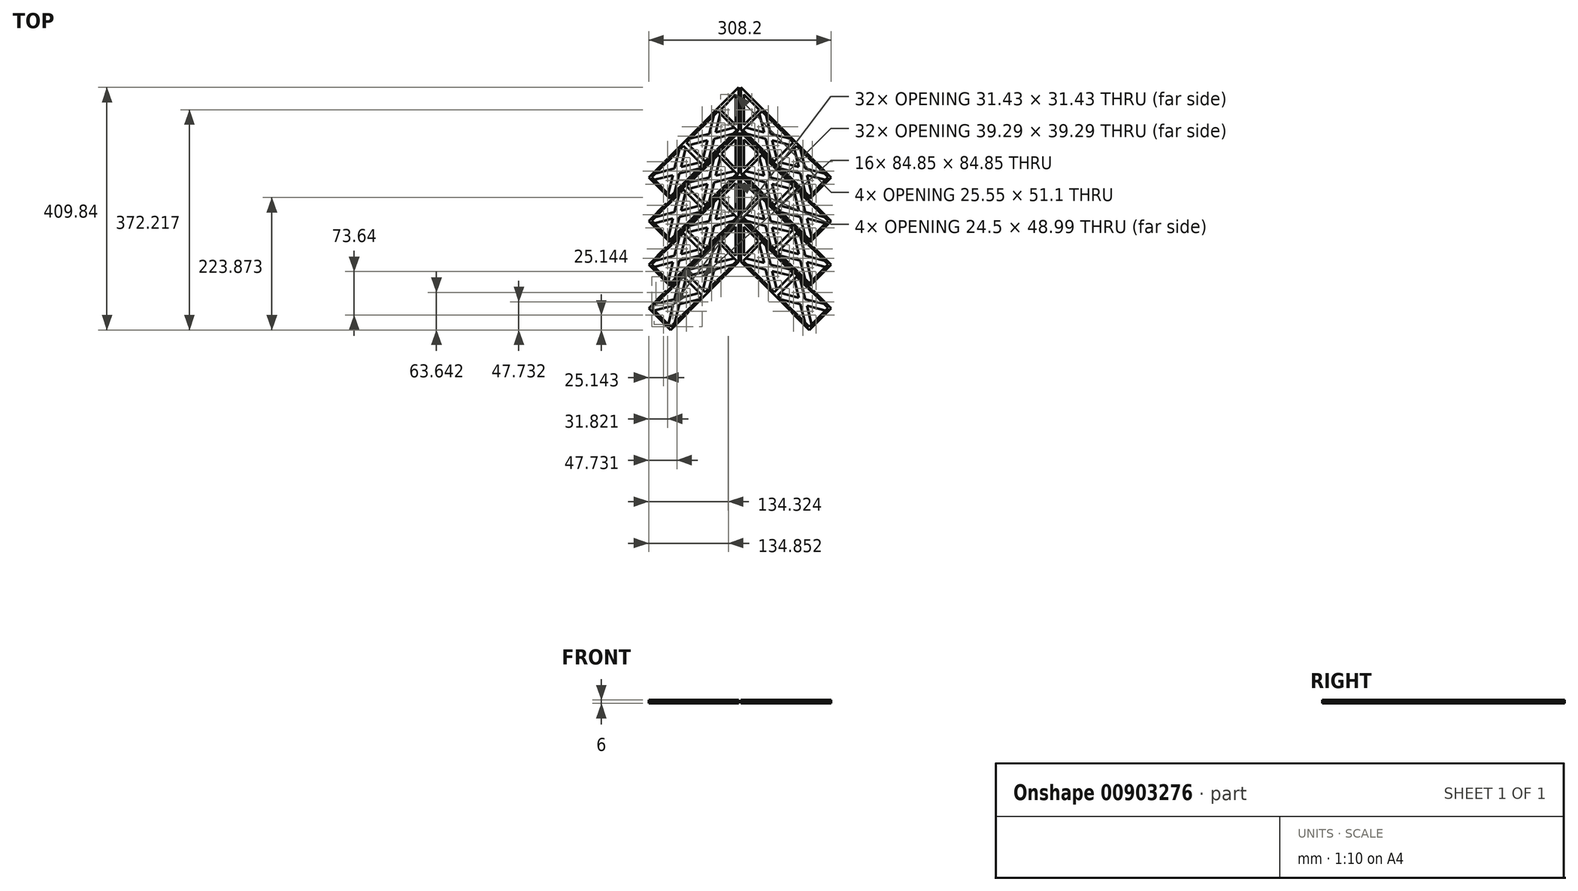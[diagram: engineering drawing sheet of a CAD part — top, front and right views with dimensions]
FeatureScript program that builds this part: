
annotation { "Feature Type Name" : "Feature", "Feature Type Description" : "" }
export const myFeature = defineFeature(function(context is Context, id is Id, definition is map)
    precondition{}
    {
        {
            var Q0;
            Q0=qCreatedBy(makeId("Top.planeOp"),FACE);
            var sketch = newSketch(context, id + "F0", { "sketchPlane" : qUnion([Q0])});
            skLineSegment(sketch, "E0", {"start": v(0, 0) * mm, "end": v(-31.82, -31.82) * mm});
            skLineSegment(sketch, "E1", {"start": v(-31.82, -31.82) * mm, "end": v(-2, -61.64) * mm});
            skLineSegment(sketch, "E2", {"start": v(-2, -208.92) * mm, "end": v(-30.76, -180.16) * mm});
            skLineSegment(sketch, "E3.MirrorCS", {"start": v(-2, -282.56) * mm, "end": v(-30.76, -253.8) * mm});
            skLineSegment(sketch, "E4", {"start": v(-31.82, -31.82) * mm, "end": v(-95.46, -95.46) * mm});
            skLineSegment(sketch, "E5", {"start": v(-2, -71.64) * mm, "end": v(-36.82, -36.82) * mm});
            skLineSegment(sketch, "E6", {"start": v(-59.7, -278.5) * mm, "end": v(-94.4, -243.8) * mm});
            skLineSegment(sketch, "E7", {"start": v(-2, -218.92) * mm, "end": v(-35.76, -185.16) * mm});
            skLineSegment(sketch, "E8", {"start": v(-37.12, -189.4) * mm, "end": v(-90.16, -242.44) * mm});
            skLineSegment(sketch, "E9", {"start": v(-58.34, -274.26) * mm, "end": v(-5.3, -221.22) * mm});
            skLineSegment(sketch, "E10", {"start": v(-37.12, -189.4) * mm, "end": v(-5.3, -221.22) * mm});
            skLineSegment(sketch, "E11", {"start": v(-58.34, -274.26) * mm, "end": v(-90.16, -242.44) * mm});
            skLineSegment(sketch, "E12", {"start": v(-37.12, -42.12) * mm, "end": v(-90.16, -95.16) * mm});
            skLineSegment(sketch, "E13", {"start": v(-90.16, -95.16) * mm, "end": v(-58.34, -126.98) * mm});
            skLineSegment(sketch, "E14", {"start": v(-58.34, -126.98) * mm, "end": v(-5.3, -73.94) * mm});
            skLineSegment(sketch, "E15", {"start": v(-5.3, -73.94) * mm, "end": v(-37.12, -42.12) * mm});
            skLineSegment(sketch, "E16", {"start": v(-5.3, -147.58) * mm, "end": v(-37.12, -115.76) * mm});
            skLineSegment(sketch, "E17", {"start": v(-37.12, -115.76) * mm, "end": v(-90.16, -168.8) * mm});
            skLineSegment(sketch, "E18", {"start": v(-90.16, -168.8) * mm, "end": v(-58.34, -200.62) * mm});
            skLineSegment(sketch, "E19", {"start": v(-58.34, -200.62) * mm, "end": v(-5.3, -147.58) * mm});
            skLineSegment(sketch, "E20.MirrorCS", {"start": v(-154.1, -154.1) * mm, "end": v(-95.46, -95.46) * mm});
            skLineSegment(sketch, "E21.MirrorCS", {"start": v(-95.76, -100.76) * mm, "end": v(-63.94, -132.58) * mm});
            skLineSegment(sketch, "E22.MirrorCS", {"start": v(-148.8, -153.8) * mm, "end": v(-95.76, -100.76) * mm});
            skLineSegment(sketch, "E23.MirrorCS", {"start": v(-116.98, -185.62) * mm, "end": v(-148.8, -153.8) * mm});
            skLineSegment(sketch, "E24.MirrorCS", {"start": v(-63.94, -132.58) * mm, "end": v(-116.98, -185.62) * mm});
            skLineSegment(sketch, "E25.MirrorCS", {"start": v(-117.28, -264.56) * mm, "end": v(-154.1, -227.74) * mm});
            skLineSegment(sketch, "E26.MirrorCS", {"start": v(-63.94, -206.22) * mm, "end": v(-116.98, -259.26) * mm});
            skLineSegment(sketch, "E27.MirrorCS", {"start": v(-95.76, -174.4) * mm, "end": v(-63.94, -206.22) * mm});
            skLineSegment(sketch, "E28.MirrorCS", {"start": v(-148.8, -227.44) * mm, "end": v(-95.76, -174.4) * mm});
            skLineSegment(sketch, "E29.MirrorCS", {"start": v(-116.98, -259.26) * mm, "end": v(-148.8, -227.44) * mm});
            skLineSegment(sketch, "E30", {"start": v(-124.35, -197.99) * mm, "end": v(-154.1, -227.74) * mm});
            skLineSegment(sketch, "E31", {"start": v(-94.4, -317.44) * mm, "end": v(-58.64, -353.2) * mm});
            skLineSegment(sketch, "E32", {"start": v(-2, -292.56) * mm, "end": v(-35.76, -258.8) * mm});
            skLineSegment(sketch, "E33", {"start": v(-37.12, -263.04) * mm, "end": v(-90.16, -316.07) * mm});
            skLineSegment(sketch, "E34", {"start": v(-5.3, -294.86) * mm, "end": v(-58.34, -347.9) * mm});
            skLineSegment(sketch, "E35", {"start": v(-90.16, -316.07) * mm, "end": v(-58.34, -347.9) * mm});
            skLineSegment(sketch, "E36", {"start": v(-5.3, -294.86) * mm, "end": v(-37.12, -263.04) * mm});
            skLineSegment(sketch, "E37.MirrorCS", {"start": v(-117.28, -338.2) * mm, "end": v(-154.1, -301.38) * mm});
            skLineSegment(sketch, "E38.MirrorCS", {"start": v(-148.8, -301.07) * mm, "end": v(-116.98, -332.9) * mm});
            skLineSegment(sketch, "E39.MirrorCS", {"start": v(-63.94, -279.86) * mm, "end": v(-116.98, -332.9) * mm});
            skLineSegment(sketch, "E40.MirrorCS", {"start": v(-63.94, -279.86) * mm, "end": v(-95.76, -248.04) * mm});
            skLineSegment(sketch, "E41.MirrorCS", {"start": v(-148.8, -301.07) * mm, "end": v(-95.76, -248.04) * mm});
            skLineSegment(sketch, "E42.MirrorCS", {"start": v(-95.76, -321.68) * mm, "end": v(-63.94, -353.5) * mm});
            skLineSegment(sketch, "E43.MirrorCS", {"start": v(-148.8, -374.71) * mm, "end": v(-95.76, -321.68) * mm});
            skLineSegment(sketch, "E44.MirrorCS", {"start": v(-116.98, -406.53) * mm, "end": v(-63.94, -353.5) * mm});
            skLineSegment(sketch, "E45.MirrorCS", {"start": v(-116.98, -406.53) * mm, "end": v(-148.8, -374.71) * mm});
            skLineSegment(sketch, "E46.MirrorCS", {"start": v(-117.28, -411.84) * mm, "end": v(-154.1, -375.02) * mm});
            skLineSegment(sketch, "E47", {"start": v(-117.28, -264.56) * mm, "end": v(-154.1, -301.38) * mm});
            skLineSegment(sketch, "E48", {"start": v(-117.28, -338.2) * mm, "end": v(-154.1, -375.02) * mm});
            skLineSegment(sketch, "E49", {"start": v(-117.28, -411.84) * mm, "end": v(-58.64, -353.2) * mm});
            skLineSegment(sketch, "E50", {"start": v(-2, -296.56) * mm, "end": v(-58.64, -353.2) * mm});
            skLineSegment(sketch, "E51", {"start": v(-2, -296.56) * mm, "end": v(-2, -2) * mm});
            skLineSegment(sketch, "E52", {"start": v(-2, -296.56) * mm, "end": v(0, -294.56) * mm});
            skLineSegment(sketch, "E53", {"start": v(-124.35, -197.99) * mm, "end": v(-123.29, -199.05) * mm});
            skLineSegment(sketch, "E54", {"start": v(-124.35, -197.99) * mm, "end": v(-117.28, -190.92) * mm});
            skLineSegment(sketch, "E55", {"start": v(-123.29, -199.05) * mm, "end": v(-2, -77.97) * mm});
            skLineSegment(sketch, "E56", {"start": v(-2, -73.31) * mm, "end": v(-118.34, -189.86) * mm});
            skLineSegment(sketch, "E57", {"start": v(-154.1, -154.1) * mm, "end": v(-117.28, -190.92) * mm});
            skLineSegment(sketch, "E58", {"start": v(-95.46, -95.46) * mm, "end": v(-59.72, -131.13) * mm});
            skLineSegment(sketch, "E59", {"start": v(-30.68, -106.6) * mm, "end": v(-2, -135.33) * mm});
            skLineSegment(sketch, "E60", {"start": v(-35.68, -111.6) * mm, "end": v(-2, -145.34) * mm});
            skLineSegment(sketch, "E61", {"start": v(-59.7, -204.86) * mm, "end": v(-94.37, -170.18) * mm});
            skLineSegment(sketch, "E62", {"start": v(-124.35, -271.63) * mm, "end": v(-123.29, -272.7) * mm});
            skLineSegment(sketch, "E63", {"start": v(-123.29, -272.7) * mm, "end": v(-2, -151.4) * mm});
            skLineSegment(sketch, "E64", {"start": v(-2, -147.16) * mm, "end": v(-118.34, -263.5) * mm});
            skLineSegment(sketch, "E65", {"start": v(-124.35, -345.27) * mm, "end": v(-123.29, -346.33) * mm});
            skLineSegment(sketch, "E66", {"start": v(-2, -225.04) * mm, "end": v(-123.29, -346.33) * mm});
            skLineSegment(sketch, "E67", {"start": v(-118.34, -337.14) * mm, "end": v(-2, -220.8) * mm});
            skLineSegment(sketch, "E68.MirrorCS", {"start": v(2, -296.56) * mm, "end": v(0, -294.56) * mm});
            skLineSegment(sketch, "E69.MirrorCS", {"start": v(2, -296.56) * mm, "end": v(2, -2) * mm});
            skLineSegment(sketch, "E70.MirrorCS", {"start": v(0, 0) * mm, "end": v(31.82, -31.82) * mm});
            skLineSegment(sketch, "E71.MirrorCS", {"start": v(31.82, -31.82) * mm, "end": v(2, -61.64) * mm});
            skLineSegment(sketch, "E72.MirrorCS", {"start": v(31.82, -31.82) * mm, "end": v(95.46, -95.46) * mm});
            skLineSegment(sketch, "E73.MirrorCS", {"start": v(154.1, -154.1) * mm, "end": v(95.46, -95.46) * mm});
            skLineSegment(sketch, "E74.MirrorCS", {"start": v(2, -71.64) * mm, "end": v(36.82, -36.82) * mm});
            skLineSegment(sketch, "E75.MirrorCS", {"start": v(2, -73.31) * mm, "end": v(118.34, -189.86) * mm});
            skLineSegment(sketch, "E76.MirrorCS", {"start": v(95.46, -95.46) * mm, "end": v(59.72, -131.13) * mm});
            skLineSegment(sketch, "E77.MirrorCS", {"start": v(154.1, -154.1) * mm, "end": v(117.28, -190.92) * mm});
            skLineSegment(sketch, "E78.MirrorCS", {"start": v(90.16, -95.16) * mm, "end": v(58.34, -126.98) * mm});
            skLineSegment(sketch, "E79.MirrorCS", {"start": v(37.12, -42.12) * mm, "end": v(90.16, -95.16) * mm});
            skLineSegment(sketch, "E80.MirrorCS", {"start": v(5.3, -73.94) * mm, "end": v(37.12, -42.12) * mm});
            skLineSegment(sketch, "E81.MirrorCS", {"start": v(58.34, -126.98) * mm, "end": v(5.3, -73.94) * mm});
            skLineSegment(sketch, "E82.MirrorCS", {"start": v(95.76, -100.76) * mm, "end": v(63.94, -132.58) * mm});
            skLineSegment(sketch, "E83.MirrorCS", {"start": v(148.8, -153.8) * mm, "end": v(95.76, -100.76) * mm});
            skLineSegment(sketch, "E84.MirrorCS", {"start": v(116.98, -185.62) * mm, "end": v(148.8, -153.8) * mm});
            skLineSegment(sketch, "E85.MirrorCS", {"start": v(63.94, -132.58) * mm, "end": v(116.98, -185.62) * mm});
            skLineSegment(sketch, "E86.MirrorCS", {"start": v(123.29, -199.05) * mm, "end": v(2, -77.97) * mm});
            skLineSegment(sketch, "E87.MirrorCS", {"start": v(30.68, -106.6) * mm, "end": v(2, -135.33) * mm});
            skLineSegment(sketch, "E88.MirrorCS", {"start": v(35.68, -111.6) * mm, "end": v(2, -145.34) * mm});
            skLineSegment(sketch, "E89.MirrorCS", {"start": v(2, -147.16) * mm, "end": v(118.34, -263.5) * mm});
            skLineSegment(sketch, "E90.MirrorCS", {"start": v(5.3, -147.58) * mm, "end": v(37.12, -115.76) * mm});
            skLineSegment(sketch, "E91.MirrorCS", {"start": v(58.34, -200.62) * mm, "end": v(5.3, -147.58) * mm});
            skLineSegment(sketch, "E92.MirrorCS", {"start": v(37.12, -115.76) * mm, "end": v(90.16, -168.8) * mm});
            skLineSegment(sketch, "E93.MirrorCS", {"start": v(90.16, -168.8) * mm, "end": v(58.34, -200.62) * mm});
            skLineSegment(sketch, "E94.MirrorCS", {"start": v(59.7, -204.86) * mm, "end": v(94.37, -170.18) * mm});
            skLineSegment(sketch, "E95.MirrorCS", {"start": v(95.76, -174.4) * mm, "end": v(63.94, -206.22) * mm});
            skLineSegment(sketch, "E96.MirrorCS", {"start": v(116.98, -259.26) * mm, "end": v(148.8, -227.44) * mm});
            skLineSegment(sketch, "E97.MirrorCS", {"start": v(148.8, -227.44) * mm, "end": v(95.76, -174.4) * mm});
            skLineSegment(sketch, "E98.MirrorCS", {"start": v(63.94, -206.22) * mm, "end": v(116.98, -259.26) * mm});
            skLineSegment(sketch, "E99.MirrorCS", {"start": v(124.35, -197.99) * mm, "end": v(154.1, -227.74) * mm});
            skLineSegment(sketch, "E100.MirrorCS", {"start": v(124.35, -197.99) * mm, "end": v(117.28, -190.92) * mm});
            skLineSegment(sketch, "E101.MirrorCS", {"start": v(117.28, -264.56) * mm, "end": v(154.1, -227.74) * mm});
            skLineSegment(sketch, "E102.MirrorCS", {"start": v(117.28, -264.56) * mm, "end": v(154.1, -301.38) * mm});
            skLineSegment(sketch, "E103.MirrorCS", {"start": v(117.28, -338.2) * mm, "end": v(154.1, -301.38) * mm});
            skLineSegment(sketch, "E104.MirrorCS", {"start": v(117.28, -338.2) * mm, "end": v(154.1, -375.02) * mm});
            skLineSegment(sketch, "E105.MirrorCS", {"start": v(117.28, -411.84) * mm, "end": v(154.1, -375.02) * mm});
            skLineSegment(sketch, "E106.MirrorCS", {"start": v(117.28, -411.84) * mm, "end": v(58.64, -353.2) * mm});
            skLineSegment(sketch, "E107.MirrorCS", {"start": v(2, -296.56) * mm, "end": v(58.64, -353.2) * mm});
            skLineSegment(sketch, "E108.MirrorCS", {"start": v(2, -208.92) * mm, "end": v(30.76, -180.16) * mm});
            skLineSegment(sketch, "E109.MirrorCS", {"start": v(2, -218.92) * mm, "end": v(35.76, -185.16) * mm});
            skLineSegment(sketch, "E110.MirrorCS", {"start": v(118.34, -337.14) * mm, "end": v(2, -220.8) * mm});
            skLineSegment(sketch, "E111.MirrorCS", {"start": v(123.29, -272.7) * mm, "end": v(2, -151.4) * mm});
            skLineSegment(sketch, "E112.MirrorCS", {"start": v(124.35, -271.63) * mm, "end": v(123.29, -272.7) * mm});
            skLineSegment(sketch, "E113.MirrorCS", {"start": v(59.7, -278.5) * mm, "end": v(94.4, -243.8) * mm});
            skLineSegment(sketch, "E114.MirrorCS", {"start": v(94.4, -317.44) * mm, "end": v(58.64, -353.2) * mm});
            skLineSegment(sketch, "E115.MirrorCS", {"start": v(2, -225.04) * mm, "end": v(123.29, -346.33) * mm});
            skLineSegment(sketch, "E116.MirrorCS", {"start": v(124.35, -345.27) * mm, "end": v(123.29, -346.33) * mm});
            skLineSegment(sketch, "E117.MirrorCS", {"start": v(2, -282.56) * mm, "end": v(30.76, -253.8) * mm});
            skLineSegment(sketch, "E118.MirrorCS", {"start": v(2, -292.56) * mm, "end": v(35.76, -258.8) * mm});
            skLineSegment(sketch, "E119.MirrorCS", {"start": v(37.12, -189.4) * mm, "end": v(5.3, -221.22) * mm});
            skLineSegment(sketch, "E120.MirrorCS", {"start": v(37.12, -189.4) * mm, "end": v(90.16, -242.44) * mm});
            skLineSegment(sketch, "E121.MirrorCS", {"start": v(58.34, -274.26) * mm, "end": v(90.16, -242.44) * mm});
            skLineSegment(sketch, "E122.MirrorCS", {"start": v(58.34, -274.26) * mm, "end": v(5.3, -221.22) * mm});
            skLineSegment(sketch, "E123.MirrorCS", {"start": v(63.94, -279.86) * mm, "end": v(95.76, -248.04) * mm});
            skLineSegment(sketch, "E124.MirrorCS", {"start": v(148.8, -301.07) * mm, "end": v(95.76, -248.04) * mm});
            skLineSegment(sketch, "E125.MirrorCS", {"start": v(148.8, -301.07) * mm, "end": v(116.98, -332.9) * mm});
            skLineSegment(sketch, "E126.MirrorCS", {"start": v(63.94, -279.86) * mm, "end": v(116.98, -332.9) * mm});
            skLineSegment(sketch, "E127.MirrorCS", {"start": v(37.12, -263.04) * mm, "end": v(90.16, -316.07) * mm});
            skLineSegment(sketch, "E128.MirrorCS", {"start": v(5.3, -294.86) * mm, "end": v(37.12, -263.04) * mm});
            skLineSegment(sketch, "E129.MirrorCS", {"start": v(5.3, -294.86) * mm, "end": v(58.34, -347.9) * mm});
            skLineSegment(sketch, "E130.MirrorCS", {"start": v(90.16, -316.07) * mm, "end": v(58.34, -347.9) * mm});
            skLineSegment(sketch, "E131.MirrorCS", {"start": v(148.8, -374.71) * mm, "end": v(95.76, -321.68) * mm});
            skLineSegment(sketch, "E132.MirrorCS", {"start": v(116.98, -406.53) * mm, "end": v(63.94, -353.5) * mm});
            skLineSegment(sketch, "E133.MirrorCS", {"start": v(95.76, -321.68) * mm, "end": v(63.94, -353.5) * mm});
            skLineSegment(sketch, "E134.MirrorCS", {"start": v(116.98, -406.53) * mm, "end": v(148.8, -374.71) * mm});
            skLineSegment(sketch, "E135.MirrorCS", {"start": v(124.35, -197.99) * mm, "end": v(123.29, -199.05) * mm});
            skSolve(sketch);
        }
        {
            var Q0;
            {var subQ0=sQuery(id+"F0.wireOp",EDGE,"E1");Q0=makeQuery(id+"F0.imprint","IMPRINT",FACE,{"disambiguationData":[TD([[makeQuery(id+"F0.imprint","IMPRINT",EDGE,{"derivedFrom":subQ0}),1.0]])]});}
            var Q1;
            {var subQ0=sQuery(id+"F0.wireOp",EDGE,"VEMovyWX-Uzcz-1f3o-4gqa-3tNphrwd6vV9");Q1=makeQuery(id+"F0.imprint","IMPRINT",FACE,{"disambiguationData":[TD([[makeQuery(id+"F0.imprint","IMPRINT",EDGE,{"derivedFrom":subQ0}),1.0]])]});}
            var Q2;
            {var subQ0=sQuery(id+"F0.wireOp",EDGE,"E1");Q2=makeQuery(id+"F0.imprint","IMPRINT",FACE,{"disambiguationData":[TD([[makeQuery(id+"F0.imprint","IMPRINT",EDGE,{"derivedFrom":subQ0}),-1.0]])]});}
            var Q3;
            {var subQ0=sQuery(id+"F0.wireOp",EDGE,"VEMovyWX-Uzcz-1f3o-4gqa-3tNphrwd6vV9");Q3=makeQuery(id+"F0.imprint","IMPRINT",FACE,{"disambiguationData":[TD([[makeQuery(id+"F0.imprint","IMPRINT",EDGE,{"derivedFrom":subQ0}),-1.0]])]});}
            var Q4;
            Q4=makeQuery(id+"F0.imprint","IMPRINT",FACE,{"disambiguationData":[TD([[makeQuery(id+"F0.imprint","IMPRINT",EDGE,{"derivedFrom":sQuery(id+"F0.wireOp",EDGE,"E31")}),-1.0]])]});
            var Q5;
            Q5=makeQuery(id+"F0.imprint","IMPRINT",FACE,{"disambiguationData":[TD([[makeQuery(id+"F0.imprint","IMPRINT",EDGE,{"derivedFrom":sQuery(id+"F0.wireOp",EDGE,"3d168247-a699-4c0e-a178-14e65d3e1d5c0.MirrorCS")}),-1.0]])]});
            var Q6;
            Q6=makeQuery(id+"F0.imprint","IMPRINT",FACE,{"disambiguationData":[TD([[makeQuery(id+"F0.imprint","IMPRINT",EDGE,{"derivedFrom":sQuery(id+"F0.wireOp",EDGE,"0Vl0EVHh-Bx7R-7UnZ-gwOp-w2B5SsMS9CPu")}),-1.0]])]});
            var Q7;
            Q7=makeQuery(id+"F0.imprint","IMPRINT",FACE,{"disambiguationData":[TD([[makeQuery(id+"F0.imprint","IMPRINT",EDGE,{"derivedFrom":sQuery(id+"F0.wireOp",EDGE,"663c4d7e-bf66-4516-a512-41397ff7d3670.MirrorCS")}),1.0]])]});
            var Q8;
            Q8=makeQuery(id+"F0.imprint","IMPRINT",FACE,{"disambiguationData":[TD([[makeQuery(id+"F0.imprint","IMPRINT",EDGE,{"derivedFrom":sQuery(id+"F0.wireOp",EDGE,"Gg0md0L4-OOCp-bCR8-Tvpl-ySR8Mx9fg5OT")}),1.0]])]});
            var Q9;
            Q9=makeQuery(id+"F0.imprint","IMPRINT",FACE,{"disambiguationData":[TD([[makeQuery(id+"F0.imprint","IMPRINT",EDGE,{"derivedFrom":sQuery(id+"F0.wireOp",EDGE,"E6")}),1.0]])]});
            var Q10;
            Q10=makeQuery(id+"F0.imprint","IMPRINT",FACE,{"disambiguationData":[TD([[makeQuery(id+"F0.imprint","IMPRINT",EDGE,{"derivedFrom":sQuery(id+"F0.wireOp",EDGE,"5ccf864e-0b62-41f3-a04c-c3cf562fed120.MirrorCS")}),-1.0]])]});
            var Q11;
            Q11=makeQuery(id+"F0.imprint","IMPRINT",FACE,{"disambiguationData":[TD([[makeQuery(id+"F0.imprint","IMPRINT",EDGE,{"derivedFrom":sQuery(id+"F0.wireOp",EDGE,"fd97eb99-5629-4112-adc0-18ec9e4a4fd80.MirrorCS")}),-1.0]])]});
            var Q12;
            {var subQ1=sQuery(id+"F0.wireOp",EDGE,"9Ym5EukE-xGI7-W4en-koQq-zlWG2HXfSDMQ");Q12=makeQuery(id+"F0.imprint","IMPRINT",FACE,{"disambiguationData":[TD([[makeQuery(id+"F0.imprint","IMPRINT",EDGE,{"derivedFrom":subQ1}),1.0]])]});}
            var Q13;
            {var subQ1=sQuery(id+"F0.wireOp",EDGE,"054f61c4-1eb1-4116-aa99-34ec667725170.MirrorCS");Q13=makeQuery(id+"F0.imprint","IMPRINT",FACE,{"disambiguationData":[TD([[makeQuery(id+"F0.imprint","IMPRINT",EDGE,{"derivedFrom":subQ1}),-1.0]])]});}
            var Q14;
            {var subQ1=sQuery(id+"F0.wireOp",EDGE,"j3KrpkpO-0uhx-MIO7-SlAU-CdksLcIEyBAU");Q14=makeQuery(id+"F0.imprint","IMPRINT",FACE,{"disambiguationData":[TD([[makeQuery(id+"F0.imprint","IMPRINT",EDGE,{"derivedFrom":subQ1}),-1.0]])]});}
            var Q15;
            {var subQ3=sQuery(id+"F0.wireOp",EDGE,"32a96095-743c-439e-8792-cb3fe6414a290.MirrorCS");Q15=makeQuery(id+"F0.imprint","IMPRINT",FACE,{"disambiguationData":[TD([[makeQuery(id+"F0.imprint","IMPRINT",EDGE,{"derivedFrom":subQ3}),1.0]])]});}
            var Q16;
            {var subQ0=sQuery(id+"F0.wireOp",EDGE,"oZT6BDRw-oxGz-oufr-c8dU-WliAKpdAL0jF");Q16=makeQuery(id+"F0.imprint","IMPRINT",FACE,{"disambiguationData":[TD([[makeQuery(id+"F0.imprint","IMPRINT",EDGE,{"derivedFrom":subQ0}),1.0]])]});}
            var Q17;
            {var subQ1=sQuery(id+"F0.wireOp",EDGE,"425ec0b5-072e-4246-bbce-0b8aed4499810.MirrorCS");Q17=makeQuery(id+"F0.imprint","IMPRINT",FACE,{"disambiguationData":[TD([[makeQuery(id+"F0.imprint","IMPRINT",EDGE,{"derivedFrom":subQ1}),-1.0]])]});}
            var Q18;
            {var subQ0=sQuery(id+"F0.wireOp",EDGE,"E2");Q18=makeQuery(id+"F0.imprint","IMPRINT",FACE,{"disambiguationData":[TD([[makeQuery(id+"F0.imprint","IMPRINT",EDGE,{"derivedFrom":subQ0}),1.0]])]});}
            var Q19;
            {var subQ2=sQuery(id+"F0.wireOp",EDGE,"61d000cf-f610-42b6-90cd-ddc3191a95350.MirrorCS");Q19=makeQuery(id+"F0.imprint","IMPRINT",FACE,{"disambiguationData":[TD([[makeQuery(id+"F0.imprint","IMPRINT",EDGE,{"derivedFrom":subQ2}),-1.0]])]});}
            var Q20;
            {var subQ0=sQuery(id+"F0.wireOp",EDGE,"q2dQMBsl-Edy5-JoF9-1dlb-58q12dl2kuox");Q20=makeQuery(id+"F0.imprint","IMPRINT",FACE,{"disambiguationData":[TD([[makeQuery(id+"F0.imprint","IMPRINT",EDGE,{"derivedFrom":subQ0}),1.0]])]});}
            var Q21;
            {var subQ0=sQuery(id+"F0.wireOp",EDGE,"j3KrpkpO-0uhx-MIO7-SlAU-CdksLcIEyBAU");Q21=makeQuery(id+"F0.imprint","IMPRINT",FACE,{"disambiguationData":[TD([[makeQuery(id+"F0.imprint","IMPRINT",EDGE,{"derivedFrom":subQ0}),1.0]])]});}
            var Q22;
            {var subQ1=sQuery(id+"F0.wireOp",EDGE,"99c90489-b881-4e89-91d4-748c54bbe8670.MirrorCS");Q22=makeQuery(id+"F0.imprint","IMPRINT",FACE,{"disambiguationData":[TD([[makeQuery(id+"F0.imprint","IMPRINT",EDGE,{"derivedFrom":subQ1}),1.0]])]});}
            var Q23;
            {var subQ3=sQuery(id+"F0.wireOp",EDGE,"oZT6BDRw-oxGz-oufr-c8dU-WliAKpdAL0jF");Q23=makeQuery(id+"F0.imprint","IMPRINT",FACE,{"disambiguationData":[TD([[makeQuery(id+"F0.imprint","IMPRINT",EDGE,{"derivedFrom":subQ3}),-1.0]])]});}
            var Q24;
            {var subQ0=sQuery(id+"F0.wireOp",EDGE,"BRIF9R1l-chW1-uXca-QMOY-jPj0UtnB7F2H");Q24=makeQuery(id+"F0.imprint","IMPRINT",FACE,{"disambiguationData":[TD([[makeQuery(id+"F0.imprint","IMPRINT",EDGE,{"derivedFrom":subQ0}),1.0]])]});}
            var Q25;
            {var subQ0=sQuery(id+"F0.wireOp",EDGE,"IwuIjNl2-2OG1-YyZA-KmhS-PqYkjRYpRXnJ");Q25=makeQuery(id+"F0.imprint","IMPRINT",FACE,{"disambiguationData":[TD([[makeQuery(id+"F0.imprint","IMPRINT",EDGE,{"derivedFrom":subQ0}),1.0]])]});}
            var Q26;
            {var subQ0=sQuery(id+"F0.wireOp",EDGE,"425ec0b5-072e-4246-bbce-0b8aed4499810.MirrorCS");Q26=makeQuery(id+"F0.imprint","IMPRINT",FACE,{"disambiguationData":[TD([[makeQuery(id+"F0.imprint","IMPRINT",EDGE,{"derivedFrom":subQ0}),1.0]])]});}
            var Q27;
            {var subQ0=sQuery(id+"F0.wireOp",EDGE,"99c90489-b881-4e89-91d4-748c54bbe8670.MirrorCS");Q27=makeQuery(id+"F0.imprint","IMPRINT",FACE,{"disambiguationData":[TD([[makeQuery(id+"F0.imprint","IMPRINT",EDGE,{"derivedFrom":subQ0}),-1.0]])]});}
            var Q28;
            {var subQ0=sQuery(id+"F0.wireOp",EDGE,"61d000cf-f610-42b6-90cd-ddc3191a95350.MirrorCS");Q28=makeQuery(id+"F0.imprint","IMPRINT",FACE,{"disambiguationData":[TD([[makeQuery(id+"F0.imprint","IMPRINT",EDGE,{"derivedFrom":subQ0}),1.0]])]});}
            var Q29;
            {var subQ0=sQuery(id+"F0.wireOp",EDGE,"1090a9d3-deac-46ea-b5c8-98feffaad39e0.MirrorCS");Q29=makeQuery(id+"F0.imprint","IMPRINT",FACE,{"disambiguationData":[TD([[makeQuery(id+"F0.imprint","IMPRINT",EDGE,{"derivedFrom":subQ0}),-1.0]])]});}
            var Q30;
            {var subQ0=sQuery(id+"F0.wireOp",EDGE,"E3.MirrorCS");Q30=makeQuery(id+"F0.imprint","IMPRINT",FACE,{"disambiguationData":[TD([[makeQuery(id+"F0.imprint","IMPRINT",EDGE,{"derivedFrom":subQ0}),1.0]])]});}
            var Q31;
            {var subQ0=sQuery(id+"F0.wireOp",EDGE,"32a96095-743c-439e-8792-cb3fe6414a290.MirrorCS");Q31=makeQuery(id+"F0.imprint","IMPRINT",FACE,{"disambiguationData":[TD([[makeQuery(id+"F0.imprint","IMPRINT",EDGE,{"derivedFrom":subQ0}),-1.0]])]});}
            var Q32;
            {var subQ1=sQuery(id+"F0.wireOp",EDGE,"E5");Q32=makeQuery(id+"F0.imprint","IMPRINT",FACE,{"disambiguationData":[TD([[makeQuery(id+"F0.imprint","IMPRINT",EDGE,{"derivedFrom":subQ1}),1.0]])]});}
            var Q33;
            {var subQ0=sQuery(id+"F0.wireOp",EDGE,"BRIF9R1l-chW1-uXca-QMOY-jPj0UtnB7F2H");Q33=makeQuery(id+"F0.imprint","IMPRINT",FACE,{"disambiguationData":[TD([[makeQuery(id+"F0.imprint","IMPRINT",EDGE,{"derivedFrom":subQ0}),-1.0]])]});}
            var Q34;
            {var subQ2=sQuery(id+"F0.wireOp",EDGE,"E20.MirrorCS");Q34=makeQuery(id+"F0.imprint","IMPRINT",FACE,{"disambiguationData":[TD([[makeQuery(id+"F0.imprint","IMPRINT",EDGE,{"derivedFrom":subQ2}),-1.0]])]});}
            var Q35;
            Q35=makeQuery(id+"F0.imprint","IMPRINT",FACE,{"disambiguationData":[TD([[makeQuery(id+"F0.imprint","IMPRINT",EDGE,{"derivedFrom":sQuery(id+"F0.wireOp",EDGE,"8NTabnAq-cU9A-DTE0-SXGj-sGRaTOjec9PT")}),1.0]])]});
            var Q36;
            {var subQ3=sQuery(id+"F0.wireOp",EDGE,"E59");Q36=makeQuery(id+"F0.imprint","IMPRINT",FACE,{"disambiguationData":[TD([[makeQuery(id+"F0.imprint","IMPRINT",EDGE,{"derivedFrom":subQ3}),1.0]])]});}
            var Q37;
            {var subQ0=sQuery(id+"F0.wireOp",EDGE,"E59");Q37=makeQuery(id+"F0.imprint","IMPRINT",FACE,{"disambiguationData":[TD([[makeQuery(id+"F0.imprint","IMPRINT",EDGE,{"derivedFrom":subQ0}),-1.0]])]});}
            var Q38;
            Q38=makeQuery(id+"F0.imprint","IMPRINT",FACE,{"disambiguationData":[TD([[makeQuery(id+"F0.imprint","IMPRINT",EDGE,{"derivedFrom":sQuery(id+"F0.wireOp",EDGE,"E26.MirrorCS")}),1.0]])]});
            var Q39;
            Q39=makeQuery(id+"F0.imprint","IMPRINT",FACE,{"disambiguationData":[TD([[makeQuery(id+"F0.imprint","IMPRINT",EDGE,{"derivedFrom":sQuery(id+"F0.wireOp",EDGE,"E16")}),-1.0]])]});
            var Q40;
            {var subQ0=sQuery(id+"F0.wireOp",EDGE,"E2");Q40=makeQuery(id+"F0.imprint","IMPRINT",FACE,{"disambiguationData":[TD([[makeQuery(id+"F0.imprint","IMPRINT",EDGE,{"derivedFrom":subQ0}),-1.0]])]});}
            var Q41;
            {var subQ1=sQuery(id+"F0.wireOp",EDGE,"E6");Q41=makeQuery(id+"F0.imprint","IMPRINT",FACE,{"disambiguationData":[TD([[makeQuery(id+"F0.imprint","IMPRINT",EDGE,{"derivedFrom":subQ1}),-1.0]])]});}
            var Q42;
            {var subQ0=sQuery(id+"F0.wireOp",EDGE,"E3.MirrorCS");Q42=makeQuery(id+"F0.imprint","IMPRINT",FACE,{"disambiguationData":[TD([[makeQuery(id+"F0.imprint","IMPRINT",EDGE,{"derivedFrom":subQ0}),-1.0]])]});}
            var Q43;
            {var subQ1=sQuery(id+"F0.wireOp",EDGE,"E31");Q43=makeQuery(id+"F0.imprint","IMPRINT",FACE,{"disambiguationData":[TD([[makeQuery(id+"F0.imprint","IMPRINT",EDGE,{"derivedFrom":subQ1}),1.0]])]});}
            var Q44;
            {var subQ3=sQuery(id+"F0.wireOp",EDGE,"E71.MirrorCS");Q44=makeQuery(id+"F0.imprint","IMPRINT",FACE,{"disambiguationData":[TD([[makeQuery(id+"F0.imprint","IMPRINT",EDGE,{"derivedFrom":subQ3}),-1.0]])]});}
            var Q45;
            {var subQ0=sQuery(id+"F0.wireOp",EDGE,"E71.MirrorCS");Q45=makeQuery(id+"F0.imprint","IMPRINT",FACE,{"disambiguationData":[TD([[makeQuery(id+"F0.imprint","IMPRINT",EDGE,{"derivedFrom":subQ0}),1.0]])]});}
            var Q46;
            {var subQ0=sQuery(id+"F0.wireOp",EDGE,"E74.MirrorCS");Q46=makeQuery(id+"F0.imprint","IMPRINT",FACE,{"disambiguationData":[TD([[makeQuery(id+"F0.imprint","IMPRINT",EDGE,{"derivedFrom":subQ0}),-1.0]])]});}
            var Q47;
            {var subQ4=sQuery(id+"F0.wireOp",EDGE,"E73.MirrorCS");Q47=makeQuery(id+"F0.imprint","IMPRINT",FACE,{"disambiguationData":[TD([[makeQuery(id+"F0.imprint","IMPRINT",EDGE,{"derivedFrom":subQ4}),1.0]])]});}
            var Q48;
            {var subQ3=sQuery(id+"F0.wireOp",EDGE,"E87.MirrorCS");Q48=makeQuery(id+"F0.imprint","IMPRINT",FACE,{"disambiguationData":[TD([[makeQuery(id+"F0.imprint","IMPRINT",EDGE,{"derivedFrom":subQ3}),-1.0]])]});}
            var Q49;
            {var subQ0=sQuery(id+"F0.wireOp",EDGE,"E87.MirrorCS");Q49=makeQuery(id+"F0.imprint","IMPRINT",FACE,{"disambiguationData":[TD([[makeQuery(id+"F0.imprint","IMPRINT",EDGE,{"derivedFrom":subQ0}),1.0]])]});}
            var Q50;
            {var subQ0=sQuery(id+"F0.wireOp",EDGE,"E88.MirrorCS");Q50=makeQuery(id+"F0.imprint","IMPRINT",FACE,{"disambiguationData":[TD([[makeQuery(id+"F0.imprint","IMPRINT",EDGE,{"derivedFrom":subQ0}),1.0]])]});}
            var Q51;
            {var subQ0=sQuery(id+"F0.wireOp",EDGE,"E94.MirrorCS");Q51=makeQuery(id+"F0.imprint","IMPRINT",FACE,{"disambiguationData":[TD([[makeQuery(id+"F0.imprint","IMPRINT",EDGE,{"derivedFrom":subQ0}),-1.0]])]});}
            var Q52;
            {var subQ0=sQuery(id+"F0.wireOp",EDGE,"E108.MirrorCS");Q52=makeQuery(id+"F0.imprint","IMPRINT",FACE,{"disambiguationData":[TD([[makeQuery(id+"F0.imprint","IMPRINT",EDGE,{"derivedFrom":subQ0}),1.0]])]});}
            var Q53;
            {var subQ0=sQuery(id+"F0.wireOp",EDGE,"E108.MirrorCS");Q53=makeQuery(id+"F0.imprint","IMPRINT",FACE,{"disambiguationData":[TD([[makeQuery(id+"F0.imprint","IMPRINT",EDGE,{"derivedFrom":subQ0}),-1.0]])]});}
            var Q54;
            {var subQ1=sQuery(id+"F0.wireOp",EDGE,"E109.MirrorCS");Q54=makeQuery(id+"F0.imprint","IMPRINT",FACE,{"disambiguationData":[TD([[makeQuery(id+"F0.imprint","IMPRINT",EDGE,{"derivedFrom":subQ1}),-1.0]])]});}
            var Q55;
            {var subQ0=sQuery(id+"F0.wireOp",EDGE,"E112.MirrorCS");Q55=makeQuery(id+"F0.imprint","IMPRINT",FACE,{"disambiguationData":[TD([[makeQuery(id+"F0.imprint","IMPRINT",EDGE,{"derivedFrom":subQ0}),1.0]])]});}
            var Q56;
            {var subQ3=sQuery(id+"F0.wireOp",EDGE,"E117.MirrorCS");Q56=makeQuery(id+"F0.imprint","IMPRINT",FACE,{"disambiguationData":[TD([[makeQuery(id+"F0.imprint","IMPRINT",EDGE,{"derivedFrom":subQ3}),1.0]])]});}
            var Q57;
            {var subQ0=sQuery(id+"F0.wireOp",EDGE,"E117.MirrorCS");Q57=makeQuery(id+"F0.imprint","IMPRINT",FACE,{"disambiguationData":[TD([[makeQuery(id+"F0.imprint","IMPRINT",EDGE,{"derivedFrom":subQ0}),-1.0]])]});}
            var Q58;
            {var subQ3=sQuery(id+"F0.wireOp",EDGE,"E107.MirrorCS");Q58=makeQuery(id+"F0.imprint","IMPRINT",FACE,{"disambiguationData":[TD([[makeQuery(id+"F0.imprint","IMPRINT",EDGE,{"derivedFrom":subQ3}),1.0]])]});}
            var Q59;
            {var subQ1=sQuery(id+"F0.wireOp",EDGE,"E105.MirrorCS");Q59=makeQuery(id+"F0.imprint","IMPRINT",FACE,{"disambiguationData":[TD([[makeQuery(id+"F0.imprint","IMPRINT",EDGE,{"derivedFrom":subQ1}),1.0]])]});}
            extrude(context, id + "F1", {"entities" : qUnion([Q0, Q1, Q2, Q3, Q4, Q5, Q6, Q7, Q8, Q9, Q10, Q11, Q12, Q13, Q14, Q15, Q16, Q17, Q18, Q19, Q20, Q21, Q22, Q23, Q24, Q25, Q26, Q27, Q28, Q29, Q30, Q31, Q32, Q33, Q34, Q35, Q36, Q37, Q38, Q39, Q40, Q41, Q42, Q43, Q44, Q45, Q46, Q47, Q48, Q49, Q50, Q51, Q52, Q53, Q54, Q55, Q56, Q57, Q58, Q59]), "depth" : 3 * mm, "offsetDistance" : 25.4 * mm});
        }
        {
            var Q0;
            Q0=makeQuery(id+"F1.opExtrude","CAP_FACE",FACE,{"disambiguationData":[OSD([sQuery(id+"F0.wireOp",EDGE,"E69.MirrorCS"),sQuery(id+"F0.wireOp",EDGE,"E104.MirrorCS"),sQuery(id+"F0.wireOp",EDGE,"E105.MirrorCS"),sQuery(id+"F0.wireOp",EDGE,"E106.MirrorCS"),sQuery(id+"F0.wireOp",EDGE,"E107.MirrorCS"),sQuery(id+"F0.wireOp",EDGE,"E115.MirrorCS"),sQuery(id+"F0.wireOp",EDGE,"E116.MirrorCS"),sQuery(id+"F0.wireOp",EDGE,"E127.MirrorCS"),sQuery(id+"F0.wireOp",EDGE,"E128.MirrorCS"),sQuery(id+"F0.wireOp",EDGE,"E129.MirrorCS"),sQuery(id+"F0.wireOp",EDGE,"E130.MirrorCS"),sQuery(id+"F0.wireOp",EDGE,"E131.MirrorCS"),sQuery(id+"F0.wireOp",EDGE,"E132.MirrorCS"),sQuery(id+"F0.wireOp",EDGE,"E133.MirrorCS"),sQuery(id+"F0.wireOp",EDGE,"E134.MirrorCS")])],"isStart":true});
            var sketch = newSketch(context, id + "F2", { "sketchPlane" : qUnion([Q0])});
            skLineSegment(sketch, "E136", {"start": v(2, 2) * mm, "end": v(154.1, 154.1) * mm});
            skLineSegment(sketch, "E137", {"start": v(154.1, 154.1) * mm, "end": v(118.34, 189.86) * mm});
            skLineSegment(sketch, "E138", {"start": v(118.34, 189.86) * mm, "end": v(2, 73.31) * mm});
            skLineSegment(sketch, "E139", {"start": v(2, 73.31) * mm, "end": v(2, 2) * mm});
            skLineSegment(sketch, "E140", {"start": v(2, 77.97) * mm, "end": v(123.29, 199.05) * mm});
            skLineSegment(sketch, "E141", {"start": v(123.29, 199.05) * mm, "end": v(124.35, 197.99) * mm});
            skLineSegment(sketch, "E142", {"start": v(124.35, 197.99) * mm, "end": v(154.1, 227.74) * mm});
            skLineSegment(sketch, "E143", {"start": v(154.1, 227.74) * mm, "end": v(118.34, 263.5) * mm});
            skLineSegment(sketch, "E144", {"start": v(118.34, 263.5) * mm, "end": v(2, 147.16) * mm});
            skLineSegment(sketch, "E145", {"start": v(2, 147.16) * mm, "end": v(2, 77.97) * mm});
            skLineSegment(sketch, "E146", {"start": v(118.34, 337.14) * mm, "end": v(2, 220.8) * mm});
            skLineSegment(sketch, "E147", {"start": v(2, 220.8) * mm, "end": v(2, 151.4) * mm});
            skLineSegment(sketch, "E148", {"start": v(2, 151.4) * mm, "end": v(123.29, 272.7) * mm});
            skLineSegment(sketch, "E149", {"start": v(123.29, 272.7) * mm, "end": v(124.35, 271.63) * mm});
            skLineSegment(sketch, "E150", {"start": v(124.35, 271.63) * mm, "end": v(154.1, 301.38) * mm});
            skLineSegment(sketch, "E151", {"start": v(154.1, 301.38) * mm, "end": v(118.34, 337.14) * mm});
            skLineSegment(sketch, "E152", {"start": v(2, 225.04) * mm, "end": v(2, 296.56) * mm});
            skLineSegment(sketch, "E153", {"start": v(2, 296.56) * mm, "end": v(117.28, 411.84) * mm});
            skLineSegment(sketch, "E154", {"start": v(117.28, 411.84) * mm, "end": v(154.1, 375.02) * mm});
            skLineSegment(sketch, "E155", {"start": v(2, 225.04) * mm, "end": v(123.29, 346.33) * mm});
            skLineSegment(sketch, "E156", {"start": v(123.29, 346.33) * mm, "end": v(124.35, 345.27) * mm});
            skLineSegment(sketch, "E157", {"start": v(124.35, 345.27) * mm, "end": v(154.1, 375.02) * mm});
            skLineSegment(sketch, "E158", {"start": v(102.63, 107.63) * mm, "end": v(141.92, 146.92) * mm});
            skLineSegment(sketch, "E159", {"start": v(144.67, 157.92) * mm, "end": v(121.1, 181.5) * mm});
            skLineSegment(sketch, "E160", {"start": v(110.1, 178.74) * mm, "end": v(70.81, 139.45) * mm});
            skLineSegment(sketch, "E161", {"start": v(68.07, 128.46) * mm, "end": v(91.64, 104.89) * mm});
            skLineSegment(sketch, "E162", {"start": v(141.92, 146.92) * mm, "end": v(110.5, 139.07) * mm});
            skLineSegment(sketch, "E163", {"start": v(70.81, 139.45) * mm, "end": v(102.25, 147.31) * mm});
            skLineSegment(sketch, "E164", {"start": v(102.63, 107.63) * mm, "end": v(110.5, 139.07) * mm});
            skLineSegment(sketch, "E165", {"start": v(91.64, 104.89) * mm, "end": v(99.5, 136.32) * mm});
            skLineSegment(sketch, "E166", {"start": v(44, 49) * mm, "end": v(83.28, 88.28) * mm});
            skLineSegment(sketch, "E167", {"start": v(86.03, 99.28) * mm, "end": v(62.46, 122.85) * mm});
            skLineSegment(sketch, "E168", {"start": v(51.46, 120.1) * mm, "end": v(12.18, 80.81) * mm});
            skLineSegment(sketch, "E169", {"start": v(9.43, 69.82) * mm, "end": v(33, 46.25) * mm});
            skLineSegment(sketch, "E170.trimOffspring", {"start": v(113.24, 150.06) * mm, "end": v(121.1, 181.5) * mm});
            skLineSegment(sketch, "E171.trimOffspring", {"start": v(99.5, 136.32) * mm, "end": v(68.07, 128.46) * mm});
            skLineSegment(sketch, "E172.trimOffspring", {"start": v(102.25, 147.31) * mm, "end": v(110.1, 178.74) * mm});
            skLineSegment(sketch, "E173.trimOffspring", {"start": v(113.24, 150.06) * mm, "end": v(144.67, 157.92) * mm});
            skLineSegment(sketch, "E174", {"start": v(86.03, 99.28) * mm, "end": v(54.6, 91.42) * mm});
            skLineSegment(sketch, "E175", {"start": v(83.28, 88.28) * mm, "end": v(51.85, 80.43) * mm});
            skLineSegment(sketch, "E176", {"start": v(51.46, 120.1) * mm, "end": v(43.6, 88.67) * mm});
            skLineSegment(sketch, "E177", {"start": v(62.46, 122.85) * mm, "end": v(54.6, 91.42) * mm});
            skLineSegment(sketch, "E178.trimOffspring", {"start": v(51.85, 80.43) * mm, "end": v(44, 49) * mm});
            skLineSegment(sketch, "E179.trimOffspring", {"start": v(40.86, 77.68) * mm, "end": v(33, 46.25) * mm});
            skLineSegment(sketch, "E180.trimOffspring", {"start": v(40.86, 77.68) * mm, "end": v(9.43, 69.82) * mm});
            skLineSegment(sketch, "E181.trimOffspring", {"start": v(43.6, 88.67) * mm, "end": v(12.18, 80.81) * mm});
            skLineSegment(sketch, "E182", {"start": v(102.63, 181.27) * mm, "end": v(141.92, 220.56) * mm});
            skLineSegment(sketch, "E183", {"start": v(144.67, 231.56) * mm, "end": v(121.1, 255.13) * mm});
            skLineSegment(sketch, "E184", {"start": v(110.1, 252.38) * mm, "end": v(70.81, 213.1) * mm});
            skLineSegment(sketch, "E185", {"start": v(68.07, 202.1) * mm, "end": v(91.64, 178.53) * mm});
            skLineSegment(sketch, "E186", {"start": v(44, 122.63) * mm, "end": v(83.28, 161.92) * mm});
            skLineSegment(sketch, "E187", {"start": v(86.03, 172.92) * mm, "end": v(62.46, 196.5) * mm});
            skLineSegment(sketch, "E188", {"start": v(51.46, 193.74) * mm, "end": v(12.18, 154.45) * mm});
            skLineSegment(sketch, "E189", {"start": v(9.43, 143.46) * mm, "end": v(33, 119.89) * mm});
            skLineSegment(sketch, "E190", {"start": v(141.92, 220.56) * mm, "end": v(110.5, 212.7) * mm});
            skLineSegment(sketch, "E191", {"start": v(144.67, 231.56) * mm, "end": v(113.24, 223.7) * mm});
            skLineSegment(sketch, "E192", {"start": v(121.1, 255.13) * mm, "end": v(113.24, 223.7) * mm});
            skLineSegment(sketch, "E193", {"start": v(110.1, 252.38) * mm, "end": v(102.25, 220.95) * mm});
            skLineSegment(sketch, "E194", {"start": v(83.28, 161.92) * mm, "end": v(51.85, 154.07) * mm});
            skLineSegment(sketch, "E195", {"start": v(86.03, 172.92) * mm, "end": v(54.6, 165.06) * mm});
            skLineSegment(sketch, "E196", {"start": v(62.46, 196.5) * mm, "end": v(54.6, 165.06) * mm});
            skLineSegment(sketch, "E197", {"start": v(51.46, 193.74) * mm, "end": v(43.6, 162.31) * mm});
            skLineSegment(sketch, "E198.trimOffspring", {"start": v(51.85, 154.07) * mm, "end": v(44, 122.63) * mm});
            skLineSegment(sketch, "E199.trimOffspring", {"start": v(40.86, 151.32) * mm, "end": v(9.43, 143.46) * mm});
            skLineSegment(sketch, "E200.trimOffspring", {"start": v(40.86, 151.32) * mm, "end": v(33, 119.89) * mm});
            skLineSegment(sketch, "E201.trimOffspring", {"start": v(43.6, 162.31) * mm, "end": v(12.18, 154.45) * mm});
            skLineSegment(sketch, "E202.trimOffspring", {"start": v(99.5, 209.96) * mm, "end": v(91.64, 178.53) * mm});
            skLineSegment(sketch, "E203.trimOffspring", {"start": v(99.5, 209.96) * mm, "end": v(68.07, 202.1) * mm});
            skLineSegment(sketch, "E204.trimOffspring", {"start": v(110.5, 212.7) * mm, "end": v(102.63, 181.27) * mm});
            skLineSegment(sketch, "E205.trimOffspring", {"start": v(102.25, 220.95) * mm, "end": v(70.81, 213.1) * mm});
            skLineSegment(sketch, "E206.MirrorCS", {"start": v(-2, 147.16) * mm, "end": v(-2, 77.97) * mm});
            skLineSegment(sketch, "E207.MirrorCS", {"start": v(-2, 73.31) * mm, "end": v(-2, 2) * mm});
            skLineSegment(sketch, "E208.MirrorCS", {"start": v(-2, 2) * mm, "end": v(-154.1, 154.1) * mm});
            skLineSegment(sketch, "E209.MirrorCS", {"start": v(-118.34, 189.86) * mm, "end": v(-2, 73.31) * mm});
            skLineSegment(sketch, "E210.MirrorCS", {"start": v(-154.1, 154.1) * mm, "end": v(-118.34, 189.86) * mm});
            skLineSegment(sketch, "E211.MirrorCS", {"start": v(-118.34, 263.5) * mm, "end": v(-2, 147.16) * mm});
            skLineSegment(sketch, "E212.MirrorCS", {"start": v(-2, 77.97) * mm, "end": v(-123.29, 199.05) * mm});
            skLineSegment(sketch, "E213.MirrorCS", {"start": v(-124.35, 197.99) * mm, "end": v(-154.1, 227.74) * mm});
            skLineSegment(sketch, "E214.MirrorCS", {"start": v(-154.1, 227.74) * mm, "end": v(-118.34, 263.5) * mm});
            skLineSegment(sketch, "E215.MirrorCS", {"start": v(-123.29, 199.05) * mm, "end": v(-124.35, 197.99) * mm});
            skLineSegment(sketch, "E216.MirrorCS", {"start": v(-9.43, 69.82) * mm, "end": v(-33, 46.25) * mm});
            skLineSegment(sketch, "E217.MirrorCS", {"start": v(-51.85, 80.43) * mm, "end": v(-44, 49) * mm});
            skLineSegment(sketch, "E218.MirrorCS", {"start": v(-40.86, 77.68) * mm, "end": v(-33, 46.25) * mm});
            skLineSegment(sketch, "E219.MirrorCS", {"start": v(-40.86, 77.68) * mm, "end": v(-9.43, 69.82) * mm});
            skLineSegment(sketch, "E220.MirrorCS", {"start": v(-43.6, 88.67) * mm, "end": v(-12.18, 80.81) * mm});
            skLineSegment(sketch, "E221.MirrorCS", {"start": v(-51.46, 120.1) * mm, "end": v(-43.6, 88.67) * mm});
            skLineSegment(sketch, "E222.MirrorCS", {"start": v(-51.46, 120.1) * mm, "end": v(-12.18, 80.81) * mm});
            skLineSegment(sketch, "E223.MirrorCS", {"start": v(-83.28, 88.28) * mm, "end": v(-51.85, 80.43) * mm});
            skLineSegment(sketch, "E224.MirrorCS", {"start": v(-44, 49) * mm, "end": v(-83.28, 88.28) * mm});
            skLineSegment(sketch, "E225.MirrorCS", {"start": v(-86.03, 99.28) * mm, "end": v(-62.46, 122.85) * mm});
            skLineSegment(sketch, "E226.MirrorCS", {"start": v(-86.03, 99.28) * mm, "end": v(-54.6, 91.42) * mm});
            skLineSegment(sketch, "E227.MirrorCS", {"start": v(-62.46, 122.85) * mm, "end": v(-54.6, 91.42) * mm});
            skLineSegment(sketch, "E228.MirrorCS", {"start": v(-68.07, 128.46) * mm, "end": v(-91.64, 104.89) * mm});
            skLineSegment(sketch, "E229.MirrorCS", {"start": v(-91.64, 104.89) * mm, "end": v(-99.5, 136.32) * mm});
            skLineSegment(sketch, "E230.MirrorCS", {"start": v(-99.5, 136.32) * mm, "end": v(-68.07, 128.46) * mm});
            skLineSegment(sketch, "E231.MirrorCS", {"start": v(-102.63, 107.63) * mm, "end": v(-110.5, 139.07) * mm});
            skLineSegment(sketch, "E232.MirrorCS", {"start": v(-102.63, 107.63) * mm, "end": v(-141.92, 146.92) * mm});
            skLineSegment(sketch, "E233.MirrorCS", {"start": v(-141.92, 146.92) * mm, "end": v(-110.5, 139.07) * mm});
            skLineSegment(sketch, "E234.MirrorCS", {"start": v(-144.67, 157.92) * mm, "end": v(-121.1, 181.5) * mm});
            skLineSegment(sketch, "E235.MirrorCS", {"start": v(-113.24, 150.06) * mm, "end": v(-121.1, 181.5) * mm});
            skLineSegment(sketch, "E236.MirrorCS", {"start": v(-110.1, 178.74) * mm, "end": v(-70.81, 139.45) * mm});
            skLineSegment(sketch, "E237.MirrorCS", {"start": v(-102.25, 147.31) * mm, "end": v(-110.1, 178.74) * mm});
            skLineSegment(sketch, "E238.MirrorCS", {"start": v(-70.81, 139.45) * mm, "end": v(-102.25, 147.31) * mm});
            skLineSegment(sketch, "E239.MirrorCS", {"start": v(-113.24, 150.06) * mm, "end": v(-144.67, 157.92) * mm});
            skLineSegment(sketch, "E240.MirrorCS", {"start": v(-9.43, 143.46) * mm, "end": v(-33, 119.89) * mm});
            skLineSegment(sketch, "E241.MirrorCS", {"start": v(-40.86, 151.32) * mm, "end": v(-33, 119.89) * mm});
            skLineSegment(sketch, "E242.MirrorCS", {"start": v(-40.86, 151.32) * mm, "end": v(-9.43, 143.46) * mm});
            skLineSegment(sketch, "E243.MirrorCS", {"start": v(-144.67, 231.56) * mm, "end": v(-121.1, 255.13) * mm});
            skLineSegment(sketch, "E244.MirrorCS", {"start": v(-144.67, 231.56) * mm, "end": v(-113.24, 223.7) * mm});
            skLineSegment(sketch, "E245.MirrorCS", {"start": v(-121.1, 255.13) * mm, "end": v(-113.24, 223.7) * mm});
            skLineSegment(sketch, "E246.MirrorCS", {"start": v(-86.03, 172.92) * mm, "end": v(-62.46, 196.5) * mm});
            skLineSegment(sketch, "E247.MirrorCS", {"start": v(-68.07, 202.1) * mm, "end": v(-91.64, 178.53) * mm});
            skLineSegment(sketch, "E248.MirrorCS", {"start": v(-99.5, 209.96) * mm, "end": v(-91.64, 178.53) * mm});
            skLineSegment(sketch, "E249.MirrorCS", {"start": v(-99.5, 209.96) * mm, "end": v(-68.07, 202.1) * mm});
            skLineSegment(sketch, "E250.MirrorCS", {"start": v(-86.03, 172.92) * mm, "end": v(-54.6, 165.06) * mm});
            skLineSegment(sketch, "E251.MirrorCS", {"start": v(-62.46, 196.5) * mm, "end": v(-54.6, 165.06) * mm});
            skLineSegment(sketch, "E252.MirrorCS", {"start": v(-83.28, 161.92) * mm, "end": v(-51.85, 154.07) * mm});
            skLineSegment(sketch, "E253.MirrorCS", {"start": v(-51.85, 154.07) * mm, "end": v(-44, 122.63) * mm});
            skLineSegment(sketch, "E254.MirrorCS", {"start": v(-44, 122.63) * mm, "end": v(-83.28, 161.92) * mm});
            skLineSegment(sketch, "E255.MirrorCS", {"start": v(-43.6, 162.31) * mm, "end": v(-12.18, 154.45) * mm});
            skLineSegment(sketch, "E256.MirrorCS", {"start": v(-51.46, 193.74) * mm, "end": v(-43.6, 162.31) * mm});
            skLineSegment(sketch, "E257.MirrorCS", {"start": v(-51.46, 193.74) * mm, "end": v(-12.18, 154.45) * mm});
            skLineSegment(sketch, "E258.MirrorCS", {"start": v(-110.5, 212.7) * mm, "end": v(-102.63, 181.27) * mm});
            skLineSegment(sketch, "E259.MirrorCS", {"start": v(-102.25, 220.95) * mm, "end": v(-70.81, 213.1) * mm});
            skLineSegment(sketch, "E260.MirrorCS", {"start": v(-110.1, 252.38) * mm, "end": v(-102.25, 220.95) * mm});
            skLineSegment(sketch, "E261.MirrorCS", {"start": v(-141.92, 220.56) * mm, "end": v(-110.5, 212.7) * mm});
            skLineSegment(sketch, "E262.MirrorCS", {"start": v(-102.63, 181.27) * mm, "end": v(-141.92, 220.56) * mm});
            skLineSegment(sketch, "E263.MirrorCS", {"start": v(-110.1, 252.38) * mm, "end": v(-70.81, 213.1) * mm});
            skLineSegment(sketch, "E264", {"start": v(33, 193.53) * mm, "end": v(9.43, 217.1) * mm});
            skLineSegment(sketch, "E265", {"start": v(12.18, 228.1) * mm, "end": v(51.46, 267.38) * mm});
            skLineSegment(sketch, "E266", {"start": v(62.46, 270.13) * mm, "end": v(86.03, 246.56) * mm});
            skLineSegment(sketch, "E267", {"start": v(83.28, 235.56) * mm, "end": v(44, 196.27) * mm});
            skLineSegment(sketch, "E268", {"start": v(70.81, 286.73) * mm, "end": v(110.1, 326.02) * mm});
            skLineSegment(sketch, "E269", {"start": v(121.1, 328.77) * mm, "end": v(144.67, 305.2) * mm});
            skLineSegment(sketch, "E270", {"start": v(141.92, 294.2) * mm, "end": v(102.63, 254.91) * mm});
            skLineSegment(sketch, "E271", {"start": v(91.64, 252.17) * mm, "end": v(68.07, 275.74) * mm});
            skLineSegment(sketch, "E272", {"start": v(141.92, 294.2) * mm, "end": v(110.5, 286.35) * mm});
            skLineSegment(sketch, "E273", {"start": v(144.67, 305.2) * mm, "end": v(113.24, 297.34) * mm});
            skLineSegment(sketch, "E274", {"start": v(121.1, 328.77) * mm, "end": v(113.24, 297.34) * mm});
            skLineSegment(sketch, "E275", {"start": v(110.1, 326.02) * mm, "end": v(102.25, 294.6) * mm});
            skLineSegment(sketch, "E276.trimOffspring", {"start": v(110.5, 286.35) * mm, "end": v(102.63, 254.91) * mm});
            skLineSegment(sketch, "E277.trimOffspring", {"start": v(102.25, 294.6) * mm, "end": v(70.81, 286.73) * mm});
            skLineSegment(sketch, "E278.trimOffspring", {"start": v(99.5, 283.6) * mm, "end": v(91.64, 252.17) * mm});
            skLineSegment(sketch, "E279.trimOffspring", {"start": v(99.5, 283.6) * mm, "end": v(68.07, 275.74) * mm});
            skLineSegment(sketch, "E280", {"start": v(62.46, 270.13) * mm, "end": v(54.6, 238.7) * mm});
            skLineSegment(sketch, "E281", {"start": v(51.46, 267.38) * mm, "end": v(43.6, 235.95) * mm});
            skLineSegment(sketch, "E282", {"start": v(83.28, 235.56) * mm, "end": v(51.85, 227.7) * mm});
            skLineSegment(sketch, "E283", {"start": v(86.03, 246.56) * mm, "end": v(54.6, 238.7) * mm});
            skLineSegment(sketch, "E284.trimOffspring", {"start": v(40.86, 224.96) * mm, "end": v(9.43, 217.1) * mm});
            skLineSegment(sketch, "E285.trimOffspring", {"start": v(51.85, 227.7) * mm, "end": v(44, 196.27) * mm});
            skLineSegment(sketch, "E286.trimOffspring", {"start": v(40.86, 224.96) * mm, "end": v(33, 193.53) * mm});
            skLineSegment(sketch, "E287.trimOffspring", {"start": v(43.6, 235.95) * mm, "end": v(12.18, 228.1) * mm});
            skLineSegment(sketch, "E288", {"start": v(44, 269.91) * mm, "end": v(83.28, 309.2) * mm});
            skLineSegment(sketch, "E289", {"start": v(86.03, 320.2) * mm, "end": v(62.46, 343.77) * mm});
            skLineSegment(sketch, "E290", {"start": v(51.46, 341.02) * mm, "end": v(12.18, 301.73) * mm});
            skLineSegment(sketch, "E291", {"start": v(9.43, 290.74) * mm, "end": v(33, 267.17) * mm});
            skLineSegment(sketch, "E292", {"start": v(91.64, 325.8) * mm, "end": v(68.07, 349.38) * mm});
            skLineSegment(sketch, "E293", {"start": v(70.81, 360.37) * mm, "end": v(110.1, 399.66) * mm});
            skLineSegment(sketch, "E294", {"start": v(121.1, 402.41) * mm, "end": v(144.67, 378.84) * mm});
            skLineSegment(sketch, "E295", {"start": v(141.92, 367.84) * mm, "end": v(102.63, 328.55) * mm});
            skLineSegment(sketch, "E296", {"start": v(141.92, 367.84) * mm, "end": v(110.5, 359.98) * mm});
            skLineSegment(sketch, "E297", {"start": v(144.67, 378.84) * mm, "end": v(113.24, 370.98) * mm});
            skLineSegment(sketch, "E298", {"start": v(110.1, 399.66) * mm, "end": v(102.25, 368.23) * mm});
            skLineSegment(sketch, "E299", {"start": v(121.1, 402.41) * mm, "end": v(113.24, 370.98) * mm});
            skLineSegment(sketch, "E300.trimOffspring", {"start": v(110.5, 359.98) * mm, "end": v(102.63, 328.55) * mm});
            skLineSegment(sketch, "E301.trimOffspring", {"start": v(99.5, 357.24) * mm, "end": v(68.07, 349.38) * mm});
            skLineSegment(sketch, "E302.trimOffspring", {"start": v(99.5, 357.24) * mm, "end": v(91.64, 325.8) * mm});
            skLineSegment(sketch, "E303.trimOffspring", {"start": v(102.25, 368.23) * mm, "end": v(70.81, 360.37) * mm});
            skLineSegment(sketch, "E304", {"start": v(83.28, 309.2) * mm, "end": v(51.85, 301.35) * mm});
            skLineSegment(sketch, "E305", {"start": v(86.03, 320.2) * mm, "end": v(54.6, 312.34) * mm});
            skLineSegment(sketch, "E306", {"start": v(62.46, 343.77) * mm, "end": v(54.6, 312.34) * mm});
            skLineSegment(sketch, "E307", {"start": v(51.46, 341.02) * mm, "end": v(43.6, 309.6) * mm});
            skLineSegment(sketch, "E308.MirrorCS", {"start": v(-2, 225.04) * mm, "end": v(-2, 296.56) * mm});
            skLineSegment(sketch, "E309.MirrorCS", {"start": v(-2, 220.8) * mm, "end": v(-2, 151.4) * mm});
            skLineSegment(sketch, "E310.MirrorCS", {"start": v(-2, 151.4) * mm, "end": v(-123.29, 272.7) * mm});
            skLineSegment(sketch, "E311.MirrorCS", {"start": v(-2, 225.04) * mm, "end": v(-123.29, 346.33) * mm});
            skLineSegment(sketch, "E312.MirrorCS", {"start": v(-2, 296.56) * mm, "end": v(-117.28, 411.84) * mm});
            skLineSegment(sketch, "E313.MirrorCS", {"start": v(-118.34, 337.14) * mm, "end": v(-2, 220.8) * mm});
            skLineSegment(sketch, "E314.MirrorCS", {"start": v(-123.29, 346.33) * mm, "end": v(-124.35, 345.27) * mm});
            skLineSegment(sketch, "E315.MirrorCS", {"start": v(-124.35, 345.27) * mm, "end": v(-154.1, 375.02) * mm});
            skLineSegment(sketch, "E316.MirrorCS", {"start": v(-123.29, 272.7) * mm, "end": v(-124.35, 271.63) * mm});
            skLineSegment(sketch, "E317.MirrorCS", {"start": v(-124.35, 271.63) * mm, "end": v(-154.1, 301.38) * mm});
            skLineSegment(sketch, "E318.MirrorCS", {"start": v(-154.1, 301.38) * mm, "end": v(-118.34, 337.14) * mm});
            skLineSegment(sketch, "E319.MirrorCS", {"start": v(-117.28, 411.84) * mm, "end": v(-154.1, 375.02) * mm});
            skLineSegment(sketch, "E320.MirrorCS", {"start": v(-33, 193.53) * mm, "end": v(-9.43, 217.1) * mm});
            skLineSegment(sketch, "E321.MirrorCS", {"start": v(-40.86, 224.96) * mm, "end": v(-9.43, 217.1) * mm});
            skLineSegment(sketch, "E322.MirrorCS", {"start": v(-40.86, 224.96) * mm, "end": v(-33, 193.53) * mm});
            skLineSegment(sketch, "E323.MirrorCS", {"start": v(-83.28, 235.56) * mm, "end": v(-44, 196.27) * mm});
            skLineSegment(sketch, "E324.MirrorCS", {"start": v(-51.85, 227.7) * mm, "end": v(-44, 196.27) * mm});
            skLineSegment(sketch, "E325.MirrorCS", {"start": v(-83.28, 235.56) * mm, "end": v(-51.85, 227.7) * mm});
            skLineSegment(sketch, "E326.MirrorCS", {"start": v(-62.46, 270.13) * mm, "end": v(-86.03, 246.56) * mm});
            skLineSegment(sketch, "E327.MirrorCS", {"start": v(-86.03, 246.56) * mm, "end": v(-54.6, 238.7) * mm});
            skLineSegment(sketch, "E328.MirrorCS", {"start": v(-62.46, 270.13) * mm, "end": v(-54.6, 238.7) * mm});
            skLineSegment(sketch, "E329.MirrorCS", {"start": v(-12.18, 228.1) * mm, "end": v(-51.46, 267.38) * mm});
            skLineSegment(sketch, "E330.MirrorCS", {"start": v(-51.46, 267.38) * mm, "end": v(-43.6, 235.95) * mm});
            skLineSegment(sketch, "E331.MirrorCS", {"start": v(-43.6, 235.95) * mm, "end": v(-12.18, 228.1) * mm});
            skLineSegment(sketch, "E332.MirrorCS", {"start": v(-91.64, 252.17) * mm, "end": v(-68.07, 275.74) * mm});
            skLineSegment(sketch, "E333.MirrorCS", {"start": v(-99.5, 283.6) * mm, "end": v(-91.64, 252.17) * mm});
            skLineSegment(sketch, "E334.MirrorCS", {"start": v(-99.5, 283.6) * mm, "end": v(-68.07, 275.74) * mm});
            skLineSegment(sketch, "E335.MirrorCS", {"start": v(-70.81, 286.73) * mm, "end": v(-110.1, 326.02) * mm});
            skLineSegment(sketch, "E336.MirrorCS", {"start": v(-102.25, 294.6) * mm, "end": v(-70.81, 286.73) * mm});
            skLineSegment(sketch, "E337.MirrorCS", {"start": v(-110.1, 326.02) * mm, "end": v(-102.25, 294.6) * mm});
            skLineSegment(sketch, "E338.MirrorCS", {"start": v(-121.1, 328.77) * mm, "end": v(-144.67, 305.2) * mm});
            skLineSegment(sketch, "E339.MirrorCS", {"start": v(-144.67, 305.2) * mm, "end": v(-113.24, 297.34) * mm});
            skLineSegment(sketch, "E340.MirrorCS", {"start": v(-121.1, 328.77) * mm, "end": v(-113.24, 297.34) * mm});
            skLineSegment(sketch, "E341.MirrorCS", {"start": v(-141.92, 294.2) * mm, "end": v(-110.5, 286.35) * mm});
            skLineSegment(sketch, "E342.MirrorCS", {"start": v(-110.5, 286.35) * mm, "end": v(-102.63, 254.91) * mm});
            skLineSegment(sketch, "E343.MirrorCS", {"start": v(-141.92, 294.2) * mm, "end": v(-102.63, 254.91) * mm});
            skLineSegment(sketch, "E344.trimOffspring", {"start": v(43.6, 309.6) * mm, "end": v(12.18, 301.73) * mm});
            skLineSegment(sketch, "E345.trimOffspring", {"start": v(51.85, 301.35) * mm, "end": v(44, 269.91) * mm});
            skLineSegment(sketch, "E346.trimOffspring", {"start": v(40.86, 298.6) * mm, "end": v(9.43, 290.74) * mm});
            skLineSegment(sketch, "E347.trimOffspring", {"start": v(40.86, 298.6) * mm, "end": v(33, 267.17) * mm});
            skLineSegment(sketch, "E348.MirrorCS", {"start": v(-9.43, 290.74) * mm, "end": v(-33, 267.17) * mm});
            skLineSegment(sketch, "E349.MirrorCS", {"start": v(-40.86, 298.6) * mm, "end": v(-33, 267.17) * mm});
            skLineSegment(sketch, "E350.MirrorCS", {"start": v(-40.86, 298.6) * mm, "end": v(-9.43, 290.74) * mm});
            skLineSegment(sketch, "E351.MirrorCS", {"start": v(-44, 269.91) * mm, "end": v(-83.28, 309.2) * mm});
            skLineSegment(sketch, "E352.MirrorCS", {"start": v(-51.85, 301.35) * mm, "end": v(-44, 269.91) * mm});
            skLineSegment(sketch, "E353.MirrorCS", {"start": v(-83.28, 309.2) * mm, "end": v(-51.85, 301.35) * mm});
            skLineSegment(sketch, "E354.MirrorCS", {"start": v(-43.6, 309.6) * mm, "end": v(-12.18, 301.73) * mm});
            skLineSegment(sketch, "E355.MirrorCS", {"start": v(-51.46, 341.02) * mm, "end": v(-12.18, 301.73) * mm});
            skLineSegment(sketch, "E356.MirrorCS", {"start": v(-51.46, 341.02) * mm, "end": v(-43.6, 309.6) * mm});
            skLineSegment(sketch, "E357.MirrorCS", {"start": v(-86.03, 320.2) * mm, "end": v(-54.6, 312.34) * mm});
            skLineSegment(sketch, "E358.MirrorCS", {"start": v(-62.46, 343.77) * mm, "end": v(-54.6, 312.34) * mm});
            skLineSegment(sketch, "E359.MirrorCS", {"start": v(-86.03, 320.2) * mm, "end": v(-62.46, 343.77) * mm});
            skLineSegment(sketch, "E360.MirrorCS", {"start": v(-91.64, 325.8) * mm, "end": v(-68.07, 349.38) * mm});
            skLineSegment(sketch, "E361.MirrorCS", {"start": v(-99.5, 357.24) * mm, "end": v(-91.64, 325.8) * mm});
            skLineSegment(sketch, "E362.MirrorCS", {"start": v(-99.5, 357.24) * mm, "end": v(-68.07, 349.38) * mm});
            skLineSegment(sketch, "E363.MirrorCS", {"start": v(-70.81, 360.37) * mm, "end": v(-110.1, 399.66) * mm});
            skLineSegment(sketch, "E364.MirrorCS", {"start": v(-102.25, 368.23) * mm, "end": v(-70.81, 360.37) * mm});
            skLineSegment(sketch, "E365.MirrorCS", {"start": v(-110.1, 399.66) * mm, "end": v(-102.25, 368.23) * mm});
            skLineSegment(sketch, "E366.MirrorCS", {"start": v(-121.1, 402.41) * mm, "end": v(-144.67, 378.84) * mm});
            skLineSegment(sketch, "E367.MirrorCS", {"start": v(-121.1, 402.41) * mm, "end": v(-113.24, 370.98) * mm});
            skLineSegment(sketch, "E368.MirrorCS", {"start": v(-144.67, 378.84) * mm, "end": v(-113.24, 370.98) * mm});
            skLineSegment(sketch, "E369.MirrorCS", {"start": v(-141.92, 367.84) * mm, "end": v(-102.63, 328.55) * mm});
            skLineSegment(sketch, "E370.MirrorCS", {"start": v(-110.5, 359.98) * mm, "end": v(-102.63, 328.55) * mm});
            skLineSegment(sketch, "E371.MirrorCS", {"start": v(-141.92, 367.84) * mm, "end": v(-110.5, 359.98) * mm});
            skSolve(sketch);
        }
        {
            var Q0;
            Q0 = qSketchRegion(id + "F2", true);
            extrude(context, id + "F3", {"entities" : qUnion([Q0]), "depth" : 3 * mm, "offsetDistance" : 25.4 * mm});
        }
        {
            var Q0;
            Q0=makeQuery(id+"F1.opExtrude","CAP_FACE",FACE,{"disambiguationData":[OSD([sQuery(id+"F0.wireOp",EDGE,"E16"),sQuery(id+"F0.wireOp",EDGE,"E17"),sQuery(id+"F0.wireOp",EDGE,"E18"),sQuery(id+"F0.wireOp",EDGE,"E19"),sQuery(id+"F0.wireOp",EDGE,"E25.MirrorCS"),sQuery(id+"F0.wireOp",EDGE,"E26.MirrorCS"),sQuery(id+"F0.wireOp",EDGE,"E27.MirrorCS"),sQuery(id+"F0.wireOp",EDGE,"E28.MirrorCS"),sQuery(id+"F0.wireOp",EDGE,"E29.MirrorCS"),sQuery(id+"F0.wireOp",EDGE,"E30"),sQuery(id+"F0.wireOp",EDGE,"E51"),sQuery(id+"F0.wireOp",EDGE,"E53"),sQuery(id+"F0.wireOp",EDGE,"E55"),sQuery(id+"F0.wireOp",EDGE,"E64")])],"isStart":false});
            var sketch = newSketch(context, id + "F4", { "sketchPlane" : qUnion([Q0])});
            skLineSegment(sketch, "E372", {"start": v(-7, -14.07) * mm, "end": v(-32.55, -39.62) * mm});
            skLineSegment(sketch, "E373", {"start": v(-32.55, -39.62) * mm, "end": v(-7, -65.18) * mm});
            skLineSegment(sketch, "E374", {"start": v(-7, -14.07) * mm, "end": v(-7, -65.18) * mm});
            skLineSegment(sketch, "E375.MirrorCS", {"start": v(7, -14.07) * mm, "end": v(7, -65.18) * mm});
            skLineSegment(sketch, "E376.MirrorCS", {"start": v(7, -14.07) * mm, "end": v(32.55, -39.62) * mm});
            skLineSegment(sketch, "E377.MirrorCS", {"start": v(32.55, -39.62) * mm, "end": v(7, -65.18) * mm});
            skLineSegment(sketch, "E378", {"start": v(-7, -90.02) * mm, "end": v(-7, -138.81) * mm});
            skLineSegment(sketch, "E379", {"start": v(-7, -90.02) * mm, "end": v(-31.4, -114.42) * mm});
            skLineSegment(sketch, "E380", {"start": v(-31.4, -114.42) * mm, "end": v(-7, -138.81) * mm});
            skLineSegment(sketch, "E381.MirrorCS", {"start": v(7, -90.02) * mm, "end": v(7, -138.81) * mm});
            skLineSegment(sketch, "E382.MirrorCS", {"start": v(7, -90.02) * mm, "end": v(31.4, -114.42) * mm});
            skLineSegment(sketch, "E383.MirrorCS", {"start": v(31.4, -114.42) * mm, "end": v(7, -138.81) * mm});
            skSolve(sketch);
        }
        {
            var Q0;
            Q0 = qSketchRegion(id + "F4", true);
            extrude(context, id + "F5", {"entities" : qUnion([Q0]), "operationType" : NewBodyOperationType.REMOVE, "oppositeDirection" : true, "depth" : 6 * mm, "offsetDistance" : 25.4 * mm});
        }
        {
            var Q0;
            Q0=makeQuery(id+"F1.opExtrude","CAP_FACE",FACE,{"disambiguationData":[OSD([sQuery(id+"F0.wireOp",EDGE,"E33"),sQuery(id+"F0.wireOp",EDGE,"E34"),sQuery(id+"F0.wireOp",EDGE,"E35"),sQuery(id+"F0.wireOp",EDGE,"E36"),sQuery(id+"F0.wireOp",EDGE,"E42.MirrorCS"),sQuery(id+"F0.wireOp",EDGE,"E43.MirrorCS"),sQuery(id+"F0.wireOp",EDGE,"E44.MirrorCS"),sQuery(id+"F0.wireOp",EDGE,"E45.MirrorCS"),sQuery(id+"F0.wireOp",EDGE,"E46.MirrorCS"),sQuery(id+"F0.wireOp",EDGE,"E48"),sQuery(id+"F0.wireOp",EDGE,"E49"),sQuery(id+"F0.wireOp",EDGE,"E50"),sQuery(id+"F0.wireOp",EDGE,"E51"),sQuery(id+"F0.wireOp",EDGE,"E65"),sQuery(id+"F0.wireOp",EDGE,"E66")])],"isStart":false});
            var sketch = newSketch(context, id + "F6", { "sketchPlane" : qUnion([Q0])});
            skLineSegment(sketch, "E384", {"start": v(-7, -163.47) * mm, "end": v(-31.5, -187.97) * mm});
            skLineSegment(sketch, "E385", {"start": v(-7, -163.47) * mm, "end": v(-7, -212.46) * mm});
            skLineSegment(sketch, "E386", {"start": v(-31.5, -187.97) * mm, "end": v(-7, -212.46) * mm});
            skLineSegment(sketch, "E387", {"start": v(-31.5, -261.6) * mm, "end": v(-7, -237.11) * mm});
            skLineSegment(sketch, "E388", {"start": v(-7, -237.11) * mm, "end": v(-7, -286.1) * mm});
            skLineSegment(sketch, "E389", {"start": v(-31.5, -261.6) * mm, "end": v(-7, -286.1) * mm});
            skLineSegment(sketch, "E390.MirrorCS", {"start": v(7, -237.11) * mm, "end": v(7, -286.1) * mm});
            skLineSegment(sketch, "E391.MirrorCS", {"start": v(7, -163.47) * mm, "end": v(7, -212.46) * mm});
            skLineSegment(sketch, "E392.MirrorCS", {"start": v(31.5, -187.97) * mm, "end": v(7, -212.46) * mm});
            skLineSegment(sketch, "E393.MirrorCS", {"start": v(7, -163.47) * mm, "end": v(31.5, -187.97) * mm});
            skLineSegment(sketch, "E394.MirrorCS", {"start": v(31.5, -261.6) * mm, "end": v(7, -237.11) * mm});
            skLineSegment(sketch, "E395.MirrorCS", {"start": v(31.5, -261.6) * mm, "end": v(7, -286.1) * mm});
            skSolve(sketch);
        }
        {
            var Q0;
            Q0 = qSketchRegion(id + "F6", true);
            extrude(context, id + "F7", {"entities" : qUnion([Q0]), "operationType" : NewBodyOperationType.REMOVE, "oppositeDirection" : true, "depth" : 6 * mm, "offsetDistance" : 25.4 * mm});
        }
    });
